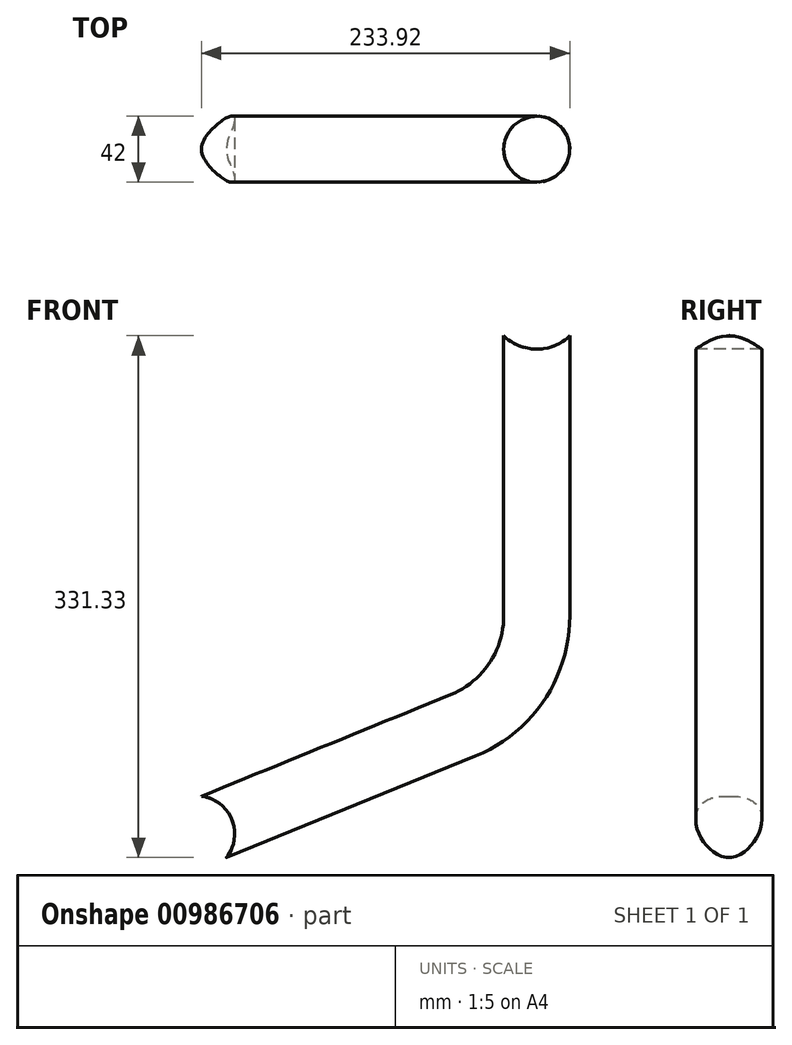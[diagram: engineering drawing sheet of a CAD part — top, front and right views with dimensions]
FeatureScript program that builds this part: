
annotation { "Feature Type Name" : "Feature", "Feature Type Description" : "" }
export const myFeature = defineFeature(function(context is Context, id is Id, definition is map)
    precondition{}
    {
        {
            var Q0;
            Q0=qCreatedBy(makeId("Front.planeOp"),FACE);
            var sketch = newSketch(context, id + "F0", { "sketchPlane" : qUnion([Q0])});
            skLineSegment(sketch, "E0", {"start": v(-246, -338) * mm, "end": v(-216, -338) * mm, "construction": true});
            skCircle(sketch, "E1", {"center": v(0, 0) * mm, "radius": 30.15 * mm});
            skCircle(sketch, "E2", {"center": v(-216, -338) * mm, "radius": 24.13 * mm});
            skLineSegment(sketch, "E3", {"start": v(-150, -250) * mm, "end": v(0, -250) * mm, "construction": true});
            skLineSegment(sketch, "E4", {"start": v(0, -199.57) * mm, "end": v(0, 0) * mm});
            skLineSegment(sketch, "E5", {"start": v(-46.7, -269.03) * mm, "end": v(-216, -338) * mm});
            skPoint(sketch, "E6.visualSharp", {"position": v(0, -250) * mm});
            skArc(sketch, "E6.filletArc", {"start": v(-46.7, -269.03) * mm, "mid": v(-12.76, -241.42) * mm, "end": v(0, -199.57) * mm});
            skLineSegment(sketch, "E7", {"start": v(0, 0) * mm, "end": v(0, -74.18) * mm, "construction": true});
            skSolve(sketch);
        }
        {
            var Q0;
            Q0=qCreatedBy(makeId("Top.planeOp"),FACE);
            var sketch = newSketch(context, id + "F1", { "sketchPlane" : qUnion([Q0])});
            skCircle(sketch, "E8", {"center": v(0, 0) * mm, "radius": 21 * mm});
            skSolve(sketch);
        }
        {
            var Q0;
            Q0=makeQuery(id+"F1.imprint","IMPRINT",FACE,{"disambiguationData":[TD([[makeQuery(id+"F1.imprint","IMPRINT",EDGE,{"derivedFrom":sQuery(id+"F1.wireOp",EDGE,"E8")}),1.0]])]});
            var Q1;
            Q1=sQuery(id+"F0.wireOp",EDGE,"E4");
            var Q2;
            Q2=sQuery(id+"F0.wireOp",EDGE,"E6.filletArc");
            var Q3;
            Q3=sQuery(id+"F0.wireOp",EDGE,"E5");
            sweep(context, id + "F2", {"profiles" : qUnion([Q0]), "path" : qUnion([Q1, Q2, Q3])});
        }
        {
            var Q0;
            Q0 = qSketchRegion(id + "F0", true);
            extrude(context, id + "F3", {"entities" : qUnion([Q0]), "operationType" : NewBodyOperationType.REMOVE, "endBound" : BoundingType.THROUGH_ALL, "oppositeDirection" : true, "depth" : 25 * mm, "offsetDistance" : 25 * mm, "hasSecondDirection" : true, "secondDirectionBound" : BoundingType.THROUGH_ALL, "secondDirectionOppositeDirection" : false, "secondDirectionDepth" : 25 * mm});
        }
    });
